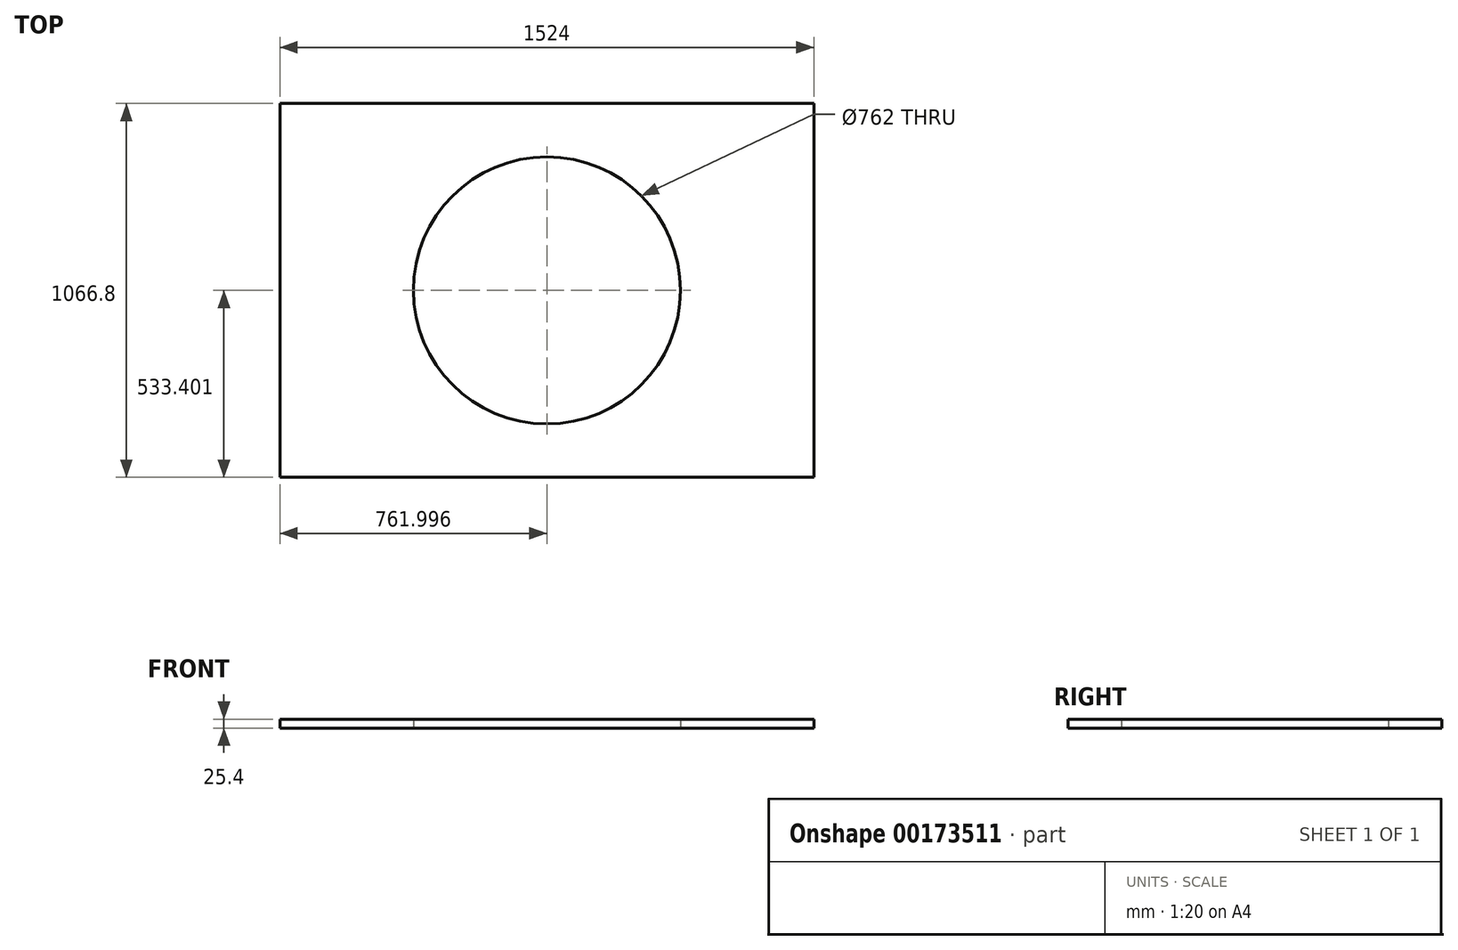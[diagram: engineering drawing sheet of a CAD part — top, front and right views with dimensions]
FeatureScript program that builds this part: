
annotation { "Feature Type Name" : "Feature", "Feature Type Description" : "" }
export const myFeature = defineFeature(function(context is Context, id is Id, definition is map)
    precondition{}
    {
        {
            var Q0;
            Q0=qCreatedBy(makeId("Top.planeOp"),FACE);
            var sketch = newSketch(context, id + "F0", { "sketchPlane" : qUnion([Q0])});
            skLineSegment(sketch, "E0.bottom", {"start": v(-1495.14, 1044.72) * mm, "end": v(28.86, 1044.72) * mm});
            skLineSegment(sketch, "E0.top", {"start": v(-1495.14, -22.08) * mm, "end": v(28.86, -22.08) * mm});
            skLineSegment(sketch, "E0.left", {"start": v(-1495.14, 1044.72) * mm, "end": v(-1495.14, -22.08) * mm});
            skLineSegment(sketch, "E0.right", {"start": v(28.86, 1044.72) * mm, "end": v(28.86, -22.08) * mm});
            skLineSegment(sketch, "E1.0", {"start": v(-733.14, 1044.72) * mm, "end": v(-733.14, -22.08) * mm});
            skLineSegment(sketch, "E2.0", {"start": v(-1495.14, 511.32) * mm, "end": v(28.86, 511.32) * mm});
            skLineSegment(sketch, "E3.0", {"start": v(-1063.34, 1044.72) * mm, "end": v(-1063.34, -22.08) * mm});
            skLineSegment(sketch, "E4.MirrorCS", {"start": v(-402.94, 1044.72) * mm, "end": v(-402.94, -22.08) * mm});
            skCircle(sketch, "E5", {"center": v(-733.14, 511.32) * mm, "radius": 381 * mm});
            skSolve(sketch);
        }
        {
            var Q0;
            Q0 = qSketchRegion(id + "F0", true);
            extrude(context, id + "F1", {"entities" : qUnion([Q0]), "depth" : 25.4 * mm});
        }
    });
